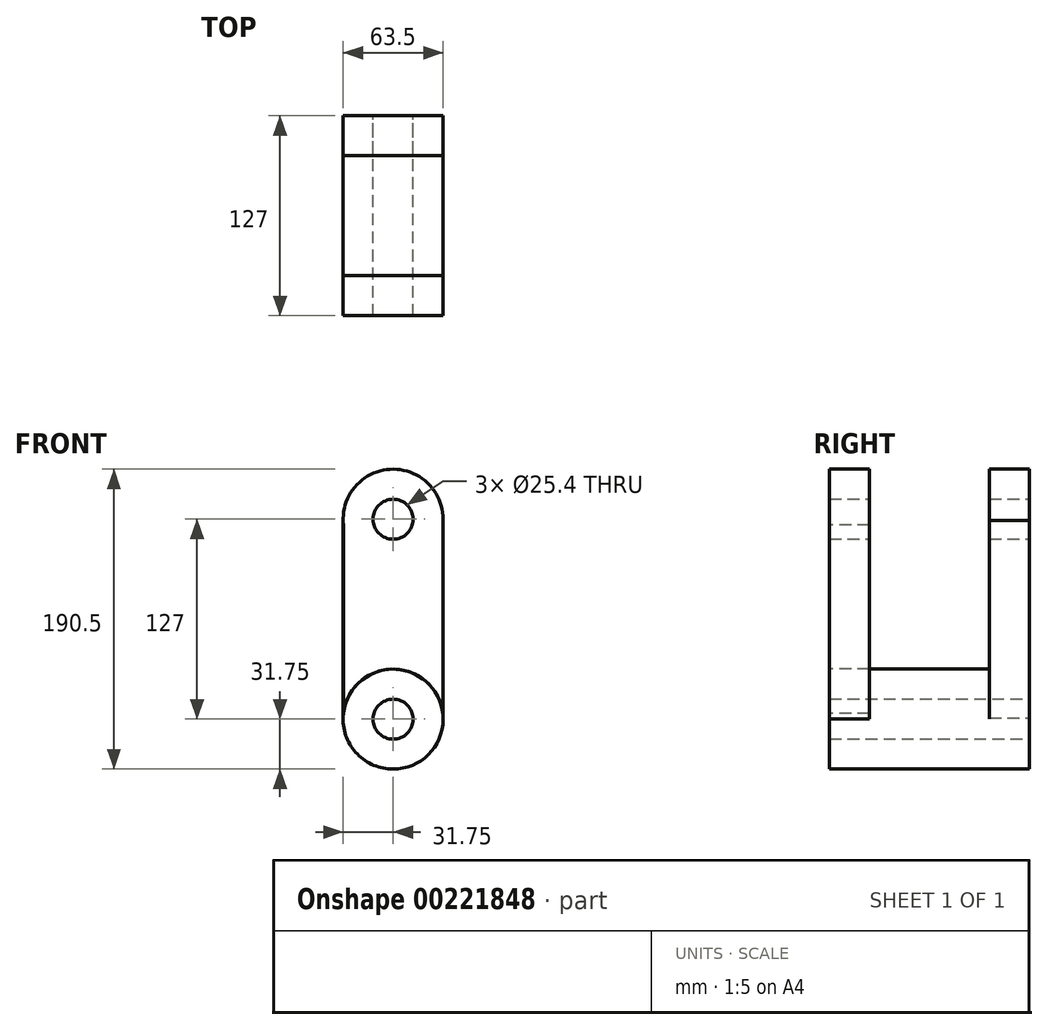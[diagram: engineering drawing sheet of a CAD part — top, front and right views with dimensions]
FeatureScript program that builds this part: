
annotation { "Feature Type Name" : "Feature", "Feature Type Description" : "" }
export const myFeature = defineFeature(function(context is Context, id is Id, definition is map)
    precondition{}
    {
        {
            var Q0;
            Q0=qCreatedBy(makeId("Front.planeOp"),FACE);
            var sketch = newSketch(context, id + "F0", { "sketchPlane" : qUnion([Q0])});
            skCircle(sketch, "E0", {"center": v(0, 0) * mm, "radius": 31.75 * mm});
            skCircle(sketch, "E1", {"center": v(0, 0) * mm, "radius": 12.7 * mm});
            skSolve(sketch);
        }
        {
            var Q0;
            Q0=makeQuery(id+"F0.imprint","IMPRINT",FACE,{"disambiguationData":[TD([[makeQuery(id+"F0.imprint","IMPRINT",EDGE,{"derivedFrom":sQuery(id+"F0.wireOp",EDGE,"E0")}),1.0]])]});
            extrude(context, id + "F1", {"entities" : qUnion([Q0]), "depth" : 127 * mm});
        }
        {
            var Q0;
            Q0=makeQuery(id+"F1.opExtrude","CAP_FACE",FACE,{"disambiguationData":[OSD([sQuery(id+"F0.wireOp",EDGE,"E0"),sQuery(id+"F0.wireOp",EDGE,"E1")])],"isStart":false});
            var sketch = newSketch(context, id + "F2", { "sketchPlane" : qUnion([Q0])});
            skArc(sketch, "E2", {"start": v(31.75, 0) * mm, "mid": v(1.9, 31.7) * mm, "end": v(-31.52, 3.79) * mm});
            skLineSegment(sketch, "E3", {"start": v(31.75, 0) * mm, "end": v(31.75, 128.42) * mm});
            skLineSegment(sketch, "E4", {"start": v(0, 0) * mm, "end": v(0, 31.75) * mm});
            skArc(sketch, "E5", {"start": v(31.75, 127) * mm, "mid": v(-1.9, 158.7) * mm, "end": v(-31.52, 123.21) * mm});
            skLineSegment(sketch, "E6", {"start": v(-31.52, 123.21) * mm, "end": v(-31.52, 0) * mm});
            skLineSegment(sketch, "E7", {"start": v(-31.52, 0) * mm, "end": v(-31.52, 130.79) * mm});
            skSolve(sketch);
        }
        {
            var Q0;
            Q0 = qSketchRegion(id + "F2", true);
            extrude(context, id + "F3", {"entities" : qUnion([Q0]), "oppositeDirection" : true, "depth" : 25.4 * mm});
        }
        {
            var Q0;
            Q0=makeQuery(id+"F1.opExtrude","CAP_FACE",FACE,{"disambiguationData":[OSD([sQuery(id+"F0.wireOp",EDGE,"E0"),sQuery(id+"F0.wireOp",EDGE,"E1")])],"isStart":true});
            var sketch = newSketch(context, id + "F4", { "sketchPlane" : qUnion([Q0])});
            skArc(sketch, "E8", {"start": v(31.74, 0.69) * mm, "mid": v(-0.34, 31.75) * mm, "end": v(-31.75, 0) * mm});
            skArc(sketch, "E9", {"start": v(31.74, 126.31) * mm, "mid": v(-0.02, 158.75) * mm, "end": v(-31.74, 126.27) * mm});
            skLineSegment(sketch, "E10", {"start": v(-31.74, 126.27) * mm, "end": v(-31.75, 0) * mm});
            skLineSegment(sketch, "E11", {"start": v(31.74, 126.31) * mm, "end": v(31.74, 0) * mm});
            skSolve(sketch);
        }
        {
            var Q0;
            Q0 = qSketchRegion(id + "F4", true);
            extrude(context, id + "F5", {"entities" : qUnion([Q0]), "operationType" : NewBodyOperationType.ADD, "oppositeDirection" : true, "depth" : 25.4 * mm});
        }
        {
            var Q0;
            Q0=makeQuery(id+"F5.boolean.opBoolean","MERGE",FACE,{"derivedFrom":[makeQuery(id+"F1.opExtrude","CAP_FACE",FACE,{"disambiguationData":[OSD([sQuery(id+"F0.wireOp",EDGE,"E0"),sQuery(id+"F0.wireOp",EDGE,"E1")])],"isStart":true}),makeQuery(id+"F5.opExtrude","CAP_FACE",FACE,{"disambiguationData":[OSD([sQuery(id+"F4.wireOp",EDGE,"E9"),sQuery(id+"F4.wireOp",EDGE,"E10"),sQuery(id+"F4.wireOp",EDGE,"E11")])],"isStart":true})]});
            var sketch = newSketch(context, id + "F6", { "sketchPlane" : qUnion([Q0])});
            skCircle(sketch, "E12", {"center": v(0, 0) * mm, "radius": 12.7 * mm});
            skCircle(sketch, "E13", {"center": v(0, 127) * mm, "radius": 12.7 * mm});
            skSolve(sketch);
        }
        {
            var Q0;
            Q0 = qSketchRegion(id + "F6", true);
            extrude(context, id + "F7", {"entities" : qUnion([Q0]), "operationType" : NewBodyOperationType.REMOVE, "oppositeDirection" : true, "depth" : 139.7 * mm});
        }
        {
            var Q0;
            Q0=makeQuery(id+"F3.opExtrude","CAP_FACE",FACE,{"disambiguationData":[OSD([sQuery(id+"F2.wireOp",EDGE,"E2"),sQuery(id+"F2.wireOp",EDGE,"E3"),sQuery(id+"F2.wireOp",EDGE,"E5"),sQuery(id+"F2.wireOp",EDGE,"E7")])],"isStart":false});
            var sketch = newSketch(context, id + "F8", { "sketchPlane" : qUnion([Q0])});
            skCircle(sketch, "E14", {"center": v(0, 127) * mm, "radius": 12.7 * mm});
            skSolve(sketch);
        }
        {
            var Q0;
            Q0 = qSketchRegion(id + "F8", true);
            extrude(context, id + "F9", {"entities" : qUnion([Q0]), "operationType" : NewBodyOperationType.REMOVE, "oppositeDirection" : true, "depth" : 38.1 * mm});
        }
    });
